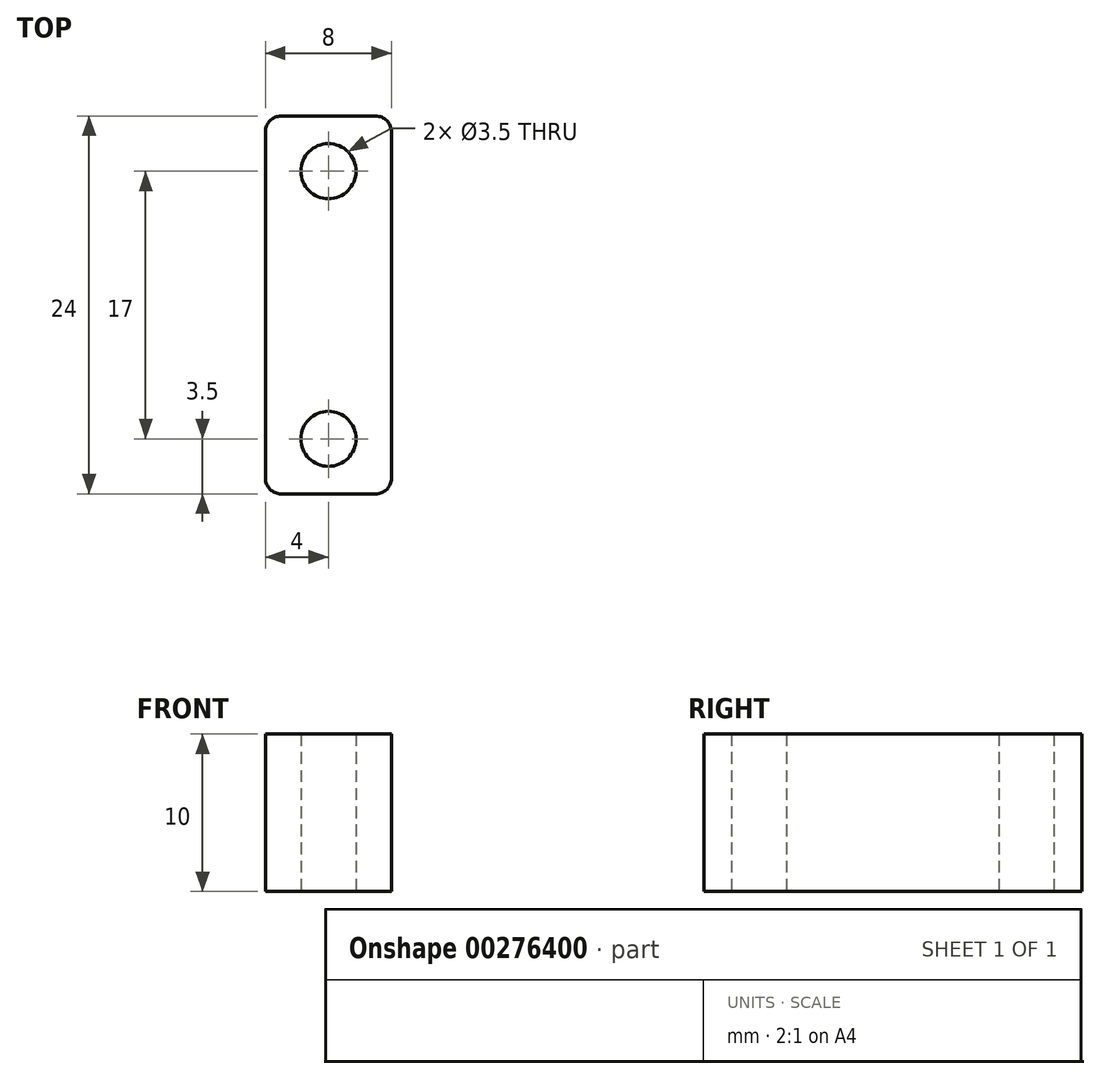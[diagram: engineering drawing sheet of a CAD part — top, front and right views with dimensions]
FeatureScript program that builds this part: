
annotation { "Feature Type Name" : "Feature", "Feature Type Description" : "" }
export const myFeature = defineFeature(function(context is Context, id is Id, definition is map)
    precondition{}
    {
        {
            var Q0;
            Q0=qCreatedBy(makeId("Top.planeOp"),FACE);
            var sketch = newSketch(context, id + "F0", { "sketchPlane" : qUnion([Q0])});
            skLineSegment(sketch, "E0.bottom", {"start": v(0, 0) * mm, "end": v(8, 0) * mm});
            skLineSegment(sketch, "E0.top", {"start": v(0, 24) * mm, "end": v(8, 24) * mm});
            skLineSegment(sketch, "E0.left", {"start": v(0, 0) * mm, "end": v(0, 24) * mm});
            skLineSegment(sketch, "E0.right", {"start": v(8, 0) * mm, "end": v(8, 24) * mm});
            skCircle(sketch, "E1", {"center": v(4, 3.5) * mm, "radius": 1.75 * mm});
            skPoint(sketch, "E1.centerSnap0", {"position": v(4, 0) * mm});
            skCircle(sketch, "E2", {"center": v(4, 20.5) * mm, "radius": 1.75 * mm});
            skSolve(sketch);
        }
        {
            var Q0;
            Q0 = qSketchRegion(id + "F0", true);
            extrude(context, id + "F1", {"entities" : qUnion([Q0]), "offsetDistance" : 25 * mm, "depth" : 10 * mm});
        }
        {
            var Q0;
            Q0=makeQuery(id+"F1.opExtrude","SWEPT_EDGE",EDGE,{"disambiguationData":[OSD([sQuery(id+"F0.wireOp",EDGE,"E0.bottom"),sQuery(id+"F0.wireOp",EDGE,"E0.right")])]});
            var Q1;
            Q1=makeQuery(id+"F1.opExtrude","SWEPT_EDGE",EDGE,{"disambiguationData":[OSD([sQuery(id+"F0.wireOp",EDGE,"E0.bottom"),sQuery(id+"F0.wireOp",EDGE,"E0.left")])]});
            var Q2;
            Q2=makeQuery(id+"F1.opExtrude","SWEPT_EDGE",EDGE,{"disambiguationData":[OSD([sQuery(id+"F0.wireOp",EDGE,"E0.top"),sQuery(id+"F0.wireOp",EDGE,"E0.left")])]});
            var Q3;
            Q3=makeQuery(id+"F1.opExtrude","SWEPT_EDGE",EDGE,{"disambiguationData":[OSD([sQuery(id+"F0.wireOp",EDGE,"E0.top"),sQuery(id+"F0.wireOp",EDGE,"E0.right")])]});
            fillet(context, id + "F2", {"entities" : qUnion([Q0, Q1, Q2, Q3]), "tangentPropagation" : true, "radius" : 1 * mm, "defaultsChanged" : false, "vertexSettings" : [], "allowEdgeOverflow" : false});
        }
    });
